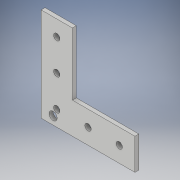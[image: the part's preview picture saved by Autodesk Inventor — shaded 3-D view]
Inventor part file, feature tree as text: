
AUTODESK INVENTOR PART (.ipt)
format: ipt  version: 2018 (Build 220112000, 112)  size: 121,856 bytes
history: native  units: in
note: dims shown in document units (in); Inventor stores cm internally (conversion verified against a paired STEP export)
features: extrude x2, sketch x2
ambient origin geometry x8: Origin, YZ Plane, XZ Plane, XY Plane, X Axis, Y Axis, Z Axis, Center Point
bodies: Solid1 (feature_tree)
feature tree (4):
  extrude  "Extrusion1"  Depth=1.0in
  extrude  "Extrusion2"  Depth=3.0in
  sketch  "Sketch1"  dims[d0=3.0in d1=1.0in]
  sketch  "Sketch2"  dims[d2=1.0in d3=3.0in d4=0.5in d5=1.0in d6=1.0in d7=1.0in d8=1.0in d9=0.2031in d10=0.125in d11=0.0in d12=0.382in d13=0.256in d14=0.26in d15=1.0in d16=0.0in]
